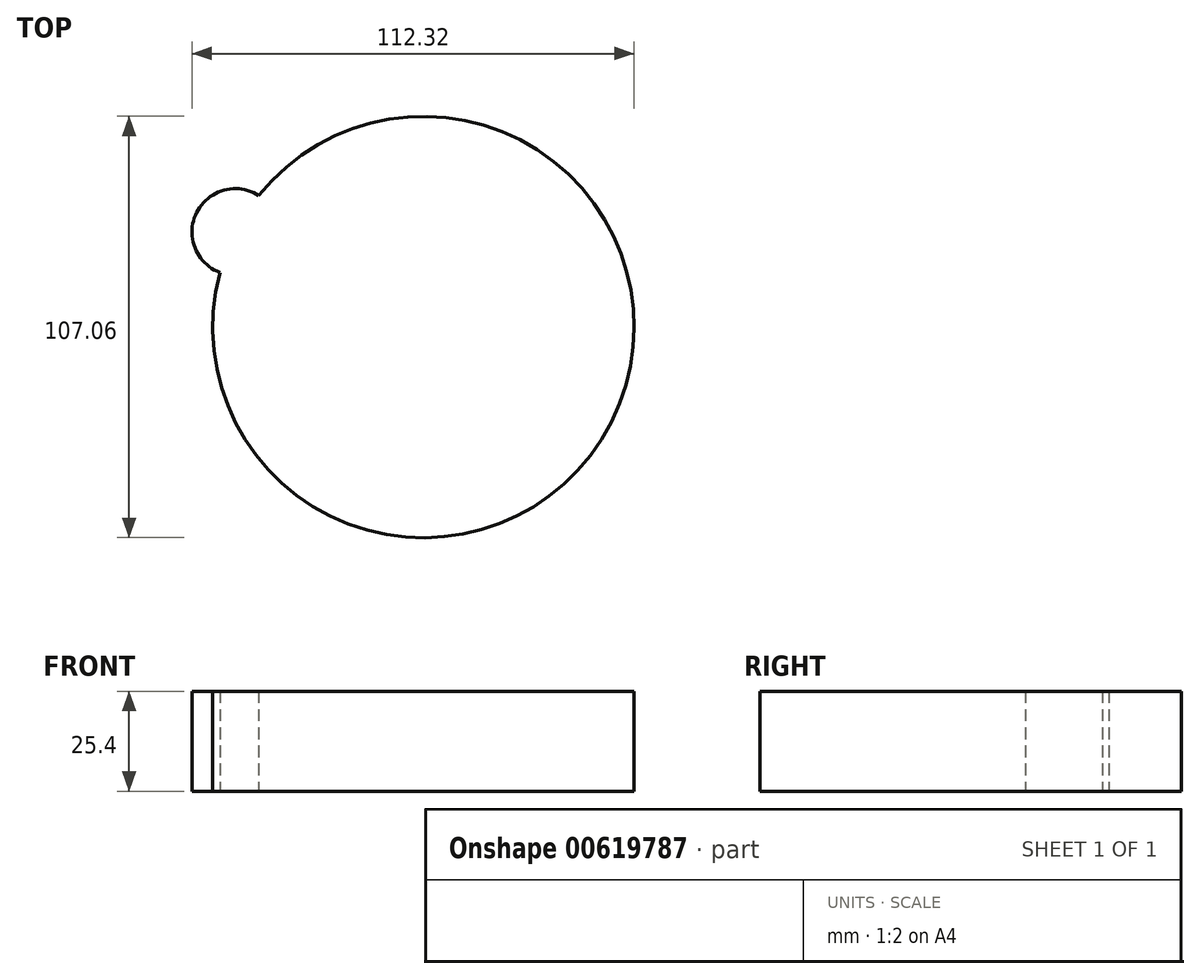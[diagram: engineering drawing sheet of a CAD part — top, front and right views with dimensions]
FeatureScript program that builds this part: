
annotation { "Feature Type Name" : "Feature", "Feature Type Description" : "" }
export const myFeature = defineFeature(function(context is Context, id is Id, definition is map)
    precondition{}
    {
        {
            var Q0;
            Q0=qCreatedBy(makeId("Top.planeOp"),FACE);
            var sketch = newSketch(context, id + "F0", { "sketchPlane" : qUnion([Q0])});
            skCircle(sketch, "E0", {"center": v(0, 0) * mm, "radius": 53.53 * mm});
            skCircle(sketch, "E1", {"center": v(-47.78, 24.14) * mm, "radius": 11 * mm});
            skSolve(sketch);
        }
        {
            var Q0;
            {var subQ0=sQuery(id+"F0.wireOp",EDGE,"E1");var subQ1=sQuery(id+"F0.wireOp",EDGE,"E0");var subQ2=makeQuery(id+"F0.imprint","INTERSECT",VERTEX,{"disambiguationData":[OD(0.0)],"derivedFrom":[subQ1,subQ0]});Q0=makeQuery(id+"F0.imprint","IMPRINT",FACE,{"disambiguationData":[TD([[makeQuery(id+"F0.imprint","IMPRINT",EDGE,{"disambiguationData":[TD([[subQ2,-1.0]])],"derivedFrom":subQ1}),1.0]])]});}
            var Q1;
            {var subQ0=sQuery(id+"F0.wireOp",EDGE,"E1");var subQ1=sQuery(id+"F0.wireOp",EDGE,"E0");var subQ2=makeQuery(id+"F0.imprint","INTERSECT",VERTEX,{"disambiguationData":[OD(0.0)],"derivedFrom":[subQ1,subQ0]});Q1=makeQuery(id+"F0.imprint","IMPRINT",FACE,{"disambiguationData":[TD([[makeQuery(id+"F0.imprint","IMPRINT",EDGE,{"disambiguationData":[TD([[subQ2,1.0]])],"derivedFrom":subQ1}),-1.0]])]});}
            var Q2;
            {var subQ0=sQuery(id+"F0.wireOp",EDGE,"E1");var subQ1=sQuery(id+"F0.wireOp",EDGE,"E0");var subQ2=makeQuery(id+"F0.imprint","INTERSECT",VERTEX,{"disambiguationData":[OD(0.0)],"derivedFrom":[subQ1,subQ0]});Q2=makeQuery(id+"F0.imprint","IMPRINT",FACE,{"disambiguationData":[TD([[makeQuery(id+"F0.imprint","IMPRINT",EDGE,{"disambiguationData":[TD([[subQ2,1.0]])],"derivedFrom":subQ1}),1.0]])]});}
            extrude(context, id + "F1", {"entities" : qUnion([Q0, Q1, Q2]), "depth" : 25.4 * mm, "offsetDistance" : 25.4 * mm});
        }
    });
